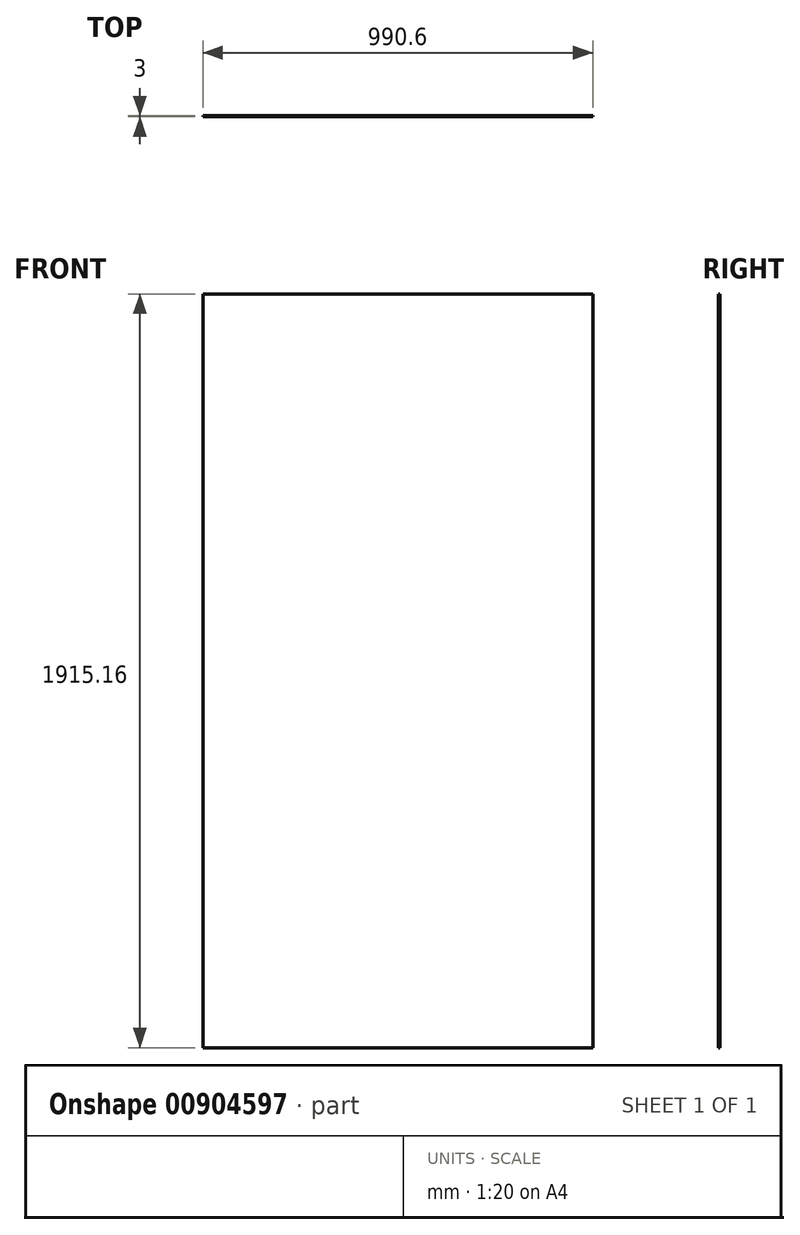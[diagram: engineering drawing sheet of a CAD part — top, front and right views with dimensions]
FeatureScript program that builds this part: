
annotation { "Feature Type Name" : "Feature", "Feature Type Description" : "" }
export const myFeature = defineFeature(function(context is Context, id is Id, definition is map)
    precondition{}
    {
        {
            var Q0;
            Q0=qCreatedBy(makeId("Front.planeOp"),FACE);
            var sketch = newSketch(context, id + "F0", { "sketchPlane" : qUnion([Q0])});
            skLineSegment(sketch, "E0.bottom", {"start": v(495.3, 957.58) * mm, "end": v(-495.3, 957.58) * mm});
            skLineSegment(sketch, "E0.top", {"start": v(495.3, -957.58) * mm, "end": v(-495.3, -957.58) * mm});
            skLineSegment(sketch, "E0.left", {"start": v(495.3, 957.58) * mm, "end": v(495.3, -957.58) * mm});
            skLineSegment(sketch, "E0.right", {"start": v(-495.3, 957.58) * mm, "end": v(-495.3, -957.58) * mm});
            skPoint(sketch, "E0.middle", {"position": v(0, 0) * mm});
            skSolve(sketch);
        }
        {
            var Q0;
            Q0 = qSketchRegion(id + "F0", true);
            extrude(context, id + "F1", {"entities" : qUnion([Q0]), "depth" : 3 * mm, "offsetDistance" : 25.4 * mm});
        }
    });
